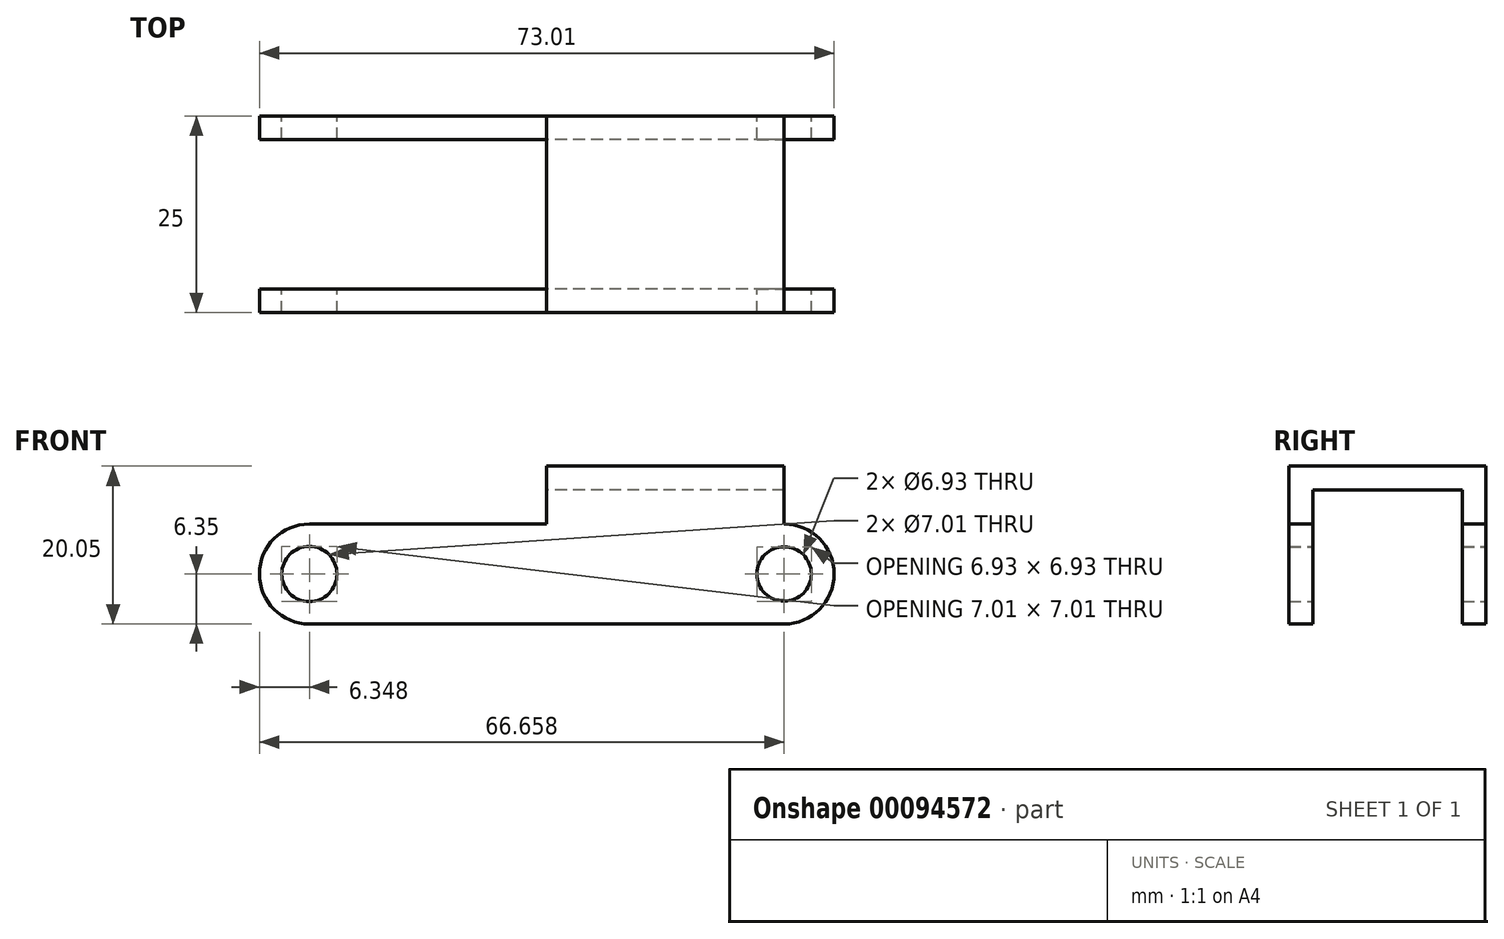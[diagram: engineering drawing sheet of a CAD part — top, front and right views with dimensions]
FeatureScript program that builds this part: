
annotation { "Feature Type Name" : "Feature", "Feature Type Description" : "" }
export const myFeature = defineFeature(function(context is Context, id is Id, definition is map)
    precondition{}
    {
        {
            var Q0;
            Q0=qCreatedBy(makeId("Front.planeOp"),FACE);
            var sketch = newSketch(context, id + "F0", { "sketchPlane" : qUnion([Q0])});
            skLineSegment(sketch, "E0", {"start": v(-30.65, 0) * mm, "end": v(29.66, 0) * mm, "construction": true});
            skArc(sketch, "E1.0.startCap", {"start": v(-30.65, -6.35) * mm, "mid": v(-37, 0) * mm, "end": v(-30.65, 6.35) * mm});
            skArc(sketch, "E1.0.endCap", {"start": v(29.66, 6.35) * mm, "mid": v(36, 0) * mm, "end": v(29.66, -6.35) * mm});
            skLineSegment(sketch, "E1.0.left", {"start": v(-30.65, 6.35) * mm, "end": v(29.66, 6.35) * mm});
            skLineSegment(sketch, "E1.0.right", {"start": v(-30.65, -6.35) * mm, "end": v(29.66, -6.35) * mm});
            skCircle(sketch, "E2", {"center": v(-30.65, 0) * mm, "radius": 3.5 * mm});
            skCircle(sketch, "E3", {"center": v(29.66, 0) * mm, "radius": 3.46 * mm});
            skLineSegment(sketch, "E4.bottom", {"start": v(-0.5, 6.35) * mm, "end": v(29.66, 6.35) * mm});
            skLineSegment(sketch, "E4.top", {"start": v(-0.5, 13.7) * mm, "end": v(29.66, 13.7) * mm});
            skLineSegment(sketch, "E4.left", {"start": v(-0.5, 6.35) * mm, "end": v(-0.5, 13.7) * mm});
            skLineSegment(sketch, "E4.right", {"start": v(29.66, 6.35) * mm, "end": v(29.66, 13.7) * mm});
            skSolve(sketch);
        }
        {
            var Q0;
            Q0 = qSketchRegion(id + "F0", true);
            extrude(context, id + "F1", {"entities" : qUnion([Q0]), "depth" : 25 * mm});
        }
        {
            var Q0;
            Q0 = qSketchRegion(id + "F0", true);
            extrude(context, id + "F2", {"entities" : qUnion([Q0]), "operationType" : NewBodyOperationType.ADD, "depth" : 25 * mm});
        }
        {
            var Q0;
            Q0=qCreatedBy(makeId("Right.planeOp"),FACE);
            var sketch = newSketch(context, id + "F3", { "sketchPlane" : qUnion([Q0])});
            skLineSegment(sketch, "E5.bottom", {"start": v(-22, 10.7) * mm, "end": v(-3, 10.7) * mm});
            skLineSegment(sketch, "E5.top", {"start": v(-22, -16.45) * mm, "end": v(-3, -16.45) * mm});
            skLineSegment(sketch, "E5.left", {"start": v(-22, 10.7) * mm, "end": v(-22, -16.45) * mm});
            skLineSegment(sketch, "E5.right", {"start": v(-3, 10.7) * mm, "end": v(-3, -16.45) * mm});
            skSolve(sketch);
        }
        {
            var Q0;
            Q0 = qSketchRegion(id + "F3", true);
            extrude(context, id + "F4", {"entities" : qUnion([Q0]), "operationType" : NewBodyOperationType.REMOVE, "endBound" : BoundingType.SYMMETRIC, "depth" : 132.9 * mm});
        }
    });
